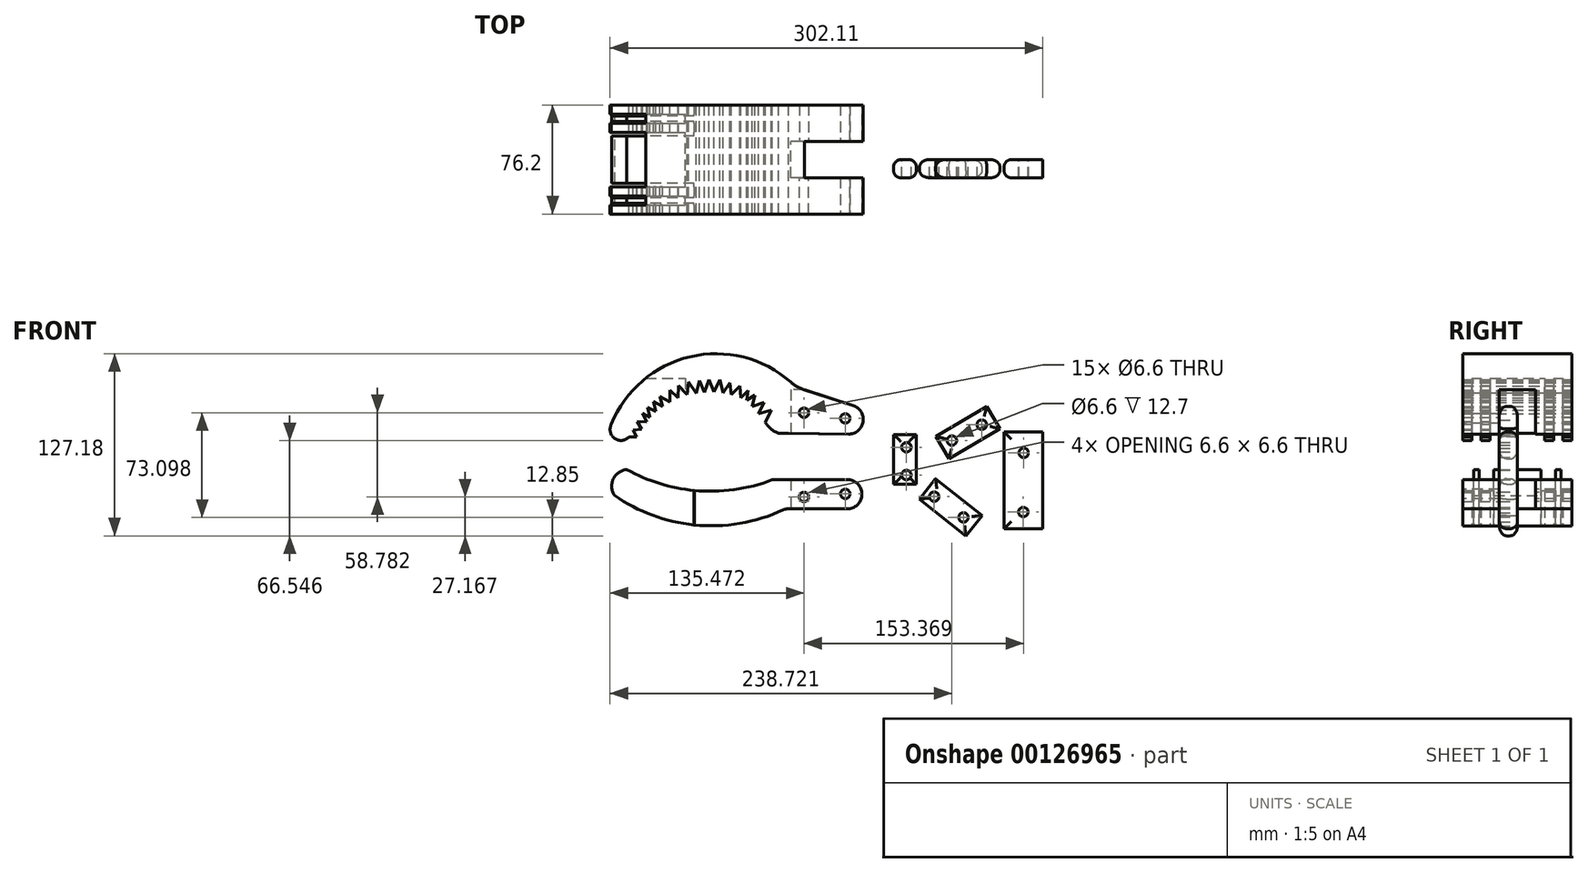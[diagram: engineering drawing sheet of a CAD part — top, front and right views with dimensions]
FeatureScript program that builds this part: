
annotation { "Feature Type Name" : "Feature", "Feature Type Description" : "" }
export const myFeature = defineFeature(function(context is Context, id is Id, definition is map)
    precondition{}
    {
        {
            var Q0;
            Q0=qCreatedBy(makeId("Front.planeOp"),FACE);
            var sketch = newSketch(context, id + "F0", { "sketchPlane" : qUnion([Q0])});
            skCircle(sketch, "E0", {"center": v(-122.1, 20.92) * mm, "radius": 7.64 * mm});
            skCircle(sketch, "E1", {"center": v(36.86, 27.9) * mm, "radius": 10.23 * mm});
            skArc(sketch, "E2", {"start": v(-123.71, 13.46) * mm, "mid": v(-118.67, 12.71) * mm, "end": v(-113.57, 12.7) * mm});
            skLineSegment(sketch, "E3", {"start": v(-113.57, 12.7) * mm, "end": v(-116.58, 15.66) * mm});
            skLineSegment(sketch, "E4", {"start": v(-116.58, 15.66) * mm, "end": v(-111.04, 15.66) * mm});
            skLineSegment(sketch, "E5", {"start": v(-111.04, 15.66) * mm, "end": v(-113.69, 20.54) * mm});
            skLineSegment(sketch, "E6", {"start": v(-113.69, 20.54) * mm, "end": v(-107.75, 21.21) * mm});
            skLineSegment(sketch, "E7", {"start": v(-107.75, 21.21) * mm, "end": v(-110.68, 26.41) * mm});
            skLineSegment(sketch, "E8", {"start": v(-110.68, 26.41) * mm, "end": v(-104.13, 26.23) * mm});
            skLineSegment(sketch, "E9", {"start": v(-104.13, 26.23) * mm, "end": v(-107.13, 32.13) * mm});
            skLineSegment(sketch, "E10", {"start": v(-107.13, 32.13) * mm, "end": v(-101.9, 29.23) * mm});
            skLineSegment(sketch, "E11", {"start": v(-101.9, 29.23) * mm, "end": v(-103.63, 36.21) * mm});
            skLineSegment(sketch, "E12", {"start": v(-103.63, 36.21) * mm, "end": v(-97.74, 33.43) * mm});
            skLineSegment(sketch, "E13", {"start": v(-97.74, 33.43) * mm, "end": v(-99.24, 40.39) * mm});
            skLineSegment(sketch, "E14", {"start": v(-99.24, 40.39) * mm, "end": v(-93.17, 36.84) * mm});
            skLineSegment(sketch, "E15", {"start": v(-93.17, 36.84) * mm, "end": v(-94.84, 44.07) * mm});
            skLineSegment(sketch, "E16", {"start": v(-94.84, 44.07) * mm, "end": v(-87.85, 40.25) * mm});
            skLineSegment(sketch, "E17", {"start": v(-87.85, 40.25) * mm, "end": v(-87.85, 48.47) * mm});
            skLineSegment(sketch, "E18", {"start": v(-87.85, 48.47) * mm, "end": v(-82.13, 43.15) * mm});
            skLineSegment(sketch, "E19", {"start": v(-82.13, 43.15) * mm, "end": v(-81.85, 51.6) * mm});
            skLineSegment(sketch, "E20", {"start": v(-81.85, 51.6) * mm, "end": v(-76.02, 45.36) * mm});
            skLineSegment(sketch, "E21", {"start": v(-76.02, 45.36) * mm, "end": v(-75.03, 53.99) * mm});
            skLineSegment(sketch, "E22", {"start": v(-75.03, 53.99) * mm, "end": v(-69.61, 46.28) * mm});
            skLineSegment(sketch, "E23", {"start": v(-69.61, 46.28) * mm, "end": v(-67.33, 55.15) * mm});
            skLineSegment(sketch, "E24", {"start": v(-67.33, 55.15) * mm, "end": v(-63.89, 46.93) * mm});
            skLineSegment(sketch, "E25", {"start": v(-63.89, 46.93) * mm, "end": v(-60.58, 55.83) * mm});
            skLineSegment(sketch, "E26", {"start": v(-60.58, 55.83) * mm, "end": v(-57.03, 47.07) * mm});
            skLineSegment(sketch, "E27", {"start": v(-57.03, 47.07) * mm, "end": v(-53, 55.7) * mm});
            skLineSegment(sketch, "E28", {"start": v(-53, 55.7) * mm, "end": v(-50.8, 46.52) * mm});
            skLineSegment(sketch, "E29", {"start": v(-50.8, 46.52) * mm, "end": v(-45.92, 53.65) * mm});
            skLineSegment(sketch, "E30", {"start": v(-45.92, 53.65) * mm, "end": v(-44.96, 45.16) * mm});
            skLineSegment(sketch, "E31", {"start": v(-44.96, 45.16) * mm, "end": v(-39.17, 51.16) * mm});
            skLineSegment(sketch, "E32", {"start": v(-39.17, 51.16) * mm, "end": v(-38.42, 43.15) * mm});
            skLineSegment(sketch, "E33", {"start": v(-38.42, 43.15) * mm, "end": v(-33.4, 47.99) * mm});
            skLineSegment(sketch, "E34", {"start": v(-33.4, 47.99) * mm, "end": v(-34.22, 41.27) * mm});
            skLineSegment(sketch, "E35", {"start": v(-34.22, 41.27) * mm, "end": v(-28.5, 44.82) * mm});
            skLineSegment(sketch, "E36", {"start": v(-28.5, 44.82) * mm, "end": v(-30.34, 36.9) * mm});
            skLineSegment(sketch, "E37", {"start": v(-30.34, 36.9) * mm, "end": v(-22.2, 39.85) * mm});
            skLineSegment(sketch, "E38", {"start": v(-22.2, 39.85) * mm, "end": v(-26.04, 31.96) * mm});
            skLineSegment(sketch, "E39", {"start": v(-26.04, 31.96) * mm, "end": v(-17.22, 34.47) * mm});
            skLineSegment(sketch, "E40", {"start": v(-17.22, 34.47) * mm, "end": v(-21.27, 26) * mm});
            skLineSegment(sketch, "E41", {"start": v(-11.97, 18.3) * mm, "end": v(-5.02, 18.3) * mm});
            skLineSegment(sketch, "E42", {"start": v(-5.02, 18.3) * mm, "end": v(36.71, 17.67) * mm});
            skArc(sketch, "E43", {"start": v(-3.6, 54) * mm, "mid": v(-73.85, 71.74) * mm, "end": v(-128.83, 24.54) * mm});
            skLineSegment(sketch, "E44", {"start": v(5.42, 48.84) * mm, "end": v(40.02, 37.63) * mm});
            skPoint(sketch, "E45.visualSharp", {"position": v(0, 50.6) * mm});
            skArc(sketch, "E45.filletArc", {"start": v(-3.6, 54) * mm, "mid": v(0.64, 50.96) * mm, "end": v(5.42, 48.84) * mm});
            skArc(sketch, "E46", {"start": v(-21.27, 26) * mm, "mid": v(-17.33, 21.28) * mm, "end": v(-11.97, 18.3) * mm});
            skArc(sketch, "E47", {"start": v(-118, -7.08) * mm, "mid": v(-127.5, -13.68) * mm, "end": v(-126.5, -25.21) * mm});
            skArc(sketch, "E48", {"start": v(-118, -7.08) * mm, "mid": v(-67.99, -21.92) * mm, "end": v(-16.4, -14.29) * mm});
            skArc(sketch, "E49", {"start": v(-126.5, -25.21) * mm, "mid": v(-68.9, -45.94) * mm, "end": v(-8.64, -35.17) * mm});
            skLineSegment(sketch, "E50", {"start": v(-16.4, -14.29) * mm, "end": v(37.68, -14.29) * mm});
            skLineSegment(sketch, "E51", {"start": v(-5.95, -34.57) * mm, "end": v(35.99, -34.57) * mm});
            skArc(sketch, "E52", {"start": v(35.99, -34.57) * mm, "mid": v(46.16, -25.2) * mm, "end": v(37.68, -14.29) * mm});
            skLineSegment(sketch, "E53.bottom", {"start": v(84.1, -17.42) * mm, "end": v(68.24, -17.42) * mm});
            skLineSegment(sketch, "E53.top", {"start": v(84.1, 17.42) * mm, "end": v(68.24, 17.42) * mm});
            skLineSegment(sketch, "E53.left", {"start": v(84.1, -17.42) * mm, "end": v(84.1, 17.42) * mm});
            skLineSegment(sketch, "E53.right", {"start": v(68.24, -17.42) * mm, "end": v(68.24, 17.42) * mm});
            skPoint(sketch, "E53.middle", {"position": v(76.17, 0) * mm});
            skLineSegment(sketch, "E54.bottom", {"start": v(172.37, 19.24) * mm, "end": v(145.4, 19.24) * mm});
            skLineSegment(sketch, "E54.top", {"start": v(172.37, -48.32) * mm, "end": v(145.4, -48.32) * mm});
            skLineSegment(sketch, "E54.left", {"start": v(172.37, 19.24) * mm, "end": v(172.37, -48.32) * mm});
            skLineSegment(sketch, "E54.right", {"start": v(145.4, 19.24) * mm, "end": v(145.4, -48.32) * mm});
            skPoint(sketch, "E54.middle", {"position": v(158.88, -14.54) * mm});
            skLineSegment(sketch, "E55.top", {"start": v(133.36, 36.98) * mm, "end": v(142.54, 21.29) * mm});
            skLineSegment(sketch, "E55.left", {"start": v(97.73, 16.15) * mm, "end": v(133.36, 36.98) * mm});
            skLineSegment(sketch, "E55.right", {"start": v(106.9, 0.45) * mm, "end": v(142.54, 21.29) * mm});
            skLineSegment(sketch, "E56.bottom", {"start": v(118.74, -53.35) * mm, "end": v(130.01, -39.1) * mm});
            skLineSegment(sketch, "E56.top", {"start": v(86.36, -27.76) * mm, "end": v(97.63, -13.5) * mm});
            skLineSegment(sketch, "E56.left", {"start": v(118.74, -53.35) * mm, "end": v(86.36, -27.76) * mm});
            skLineSegment(sketch, "E56.right", {"start": v(130.01, -39.1) * mm, "end": v(97.63, -13.5) * mm});
            skLineSegment(sketch, "E57", {"start": v(97.73, 16.15) * mm, "end": v(106.9, 0.45) * mm});
            skPoint(sketch, "E58.visualSharp", {"position": v(-7.38, -34.57) * mm});
            skArc(sketch, "E58.filletArc", {"start": v(-5.95, -34.57) * mm, "mid": v(-7.33, -34.72) * mm, "end": v(-8.64, -35.17) * mm});
            skPoint(sketch, "E59", {"position": v(5.73, 32.6) * mm});
            skPoint(sketch, "E60", {"position": v(5.73, -26.18) * mm});
            skPoint(sketch, "E61", {"position": v(77.23, 8.5) * mm});
            skPoint(sketch, "E62", {"position": v(77.23, -10.88) * mm});
            skPoint(sketch, "E63", {"position": v(108.98, 13.2) * mm});
            skPoint(sketch, "E64", {"position": v(129.86, 24.28) * mm});
            skPoint(sketch, "E65", {"position": v(96.62, -26.01) * mm});
            skPoint(sketch, "E66", {"position": v(117.08, -40.5) * mm});
            skPoint(sketch, "E67", {"position": v(159.1, 4.57) * mm});
            skPoint(sketch, "E68", {"position": v(158.87, -36.77) * mm});
            skSolve(sketch);
        }
        {
            var Q0;
            Q0=qCreatedBy(makeId("Right.planeOp"),FACE);
            var sketch = newSketch(context, id + "F1", { "sketchPlane" : qUnion([Q0])});
            skLineSegment(sketch, "E69.bottom", {"start": v(19.05, 29.98) * mm, "end": v(-19.05, 29.98) * mm});
            skLineSegment(sketch, "E69.top", {"start": v(19.05, -29.98) * mm, "end": v(-19.05, -29.98) * mm});
            skLineSegment(sketch, "E69.left", {"start": v(19.05, 29.98) * mm, "end": v(19.05, -29.98) * mm});
            skLineSegment(sketch, "E69.right", {"start": v(-19.05, 29.98) * mm, "end": v(-19.05, -29.98) * mm});
            skPoint(sketch, "E69.middle", {"position": v(0, 0) * mm});
            skLineSegment(sketch, "E70.bottom", {"start": v(-31.75, 29.98) * mm, "end": v(-25.4, 29.98) * mm});
            skLineSegment(sketch, "E70.top", {"start": v(-31.75, -29.98) * mm, "end": v(-25.4, -29.98) * mm});
            skLineSegment(sketch, "E70.left", {"start": v(-31.75, 29.98) * mm, "end": v(-31.75, -29.98) * mm});
            skLineSegment(sketch, "E70.right", {"start": v(-25.4, 29.98) * mm, "end": v(-25.4, -29.98) * mm});
            skPoint(sketch, "E70.middle", {"position": v(-28.58, 0) * mm});
            skLineSegment(sketch, "E71.bottom", {"start": v(25.4, 29.98) * mm, "end": v(31.75, 29.98) * mm});
            skLineSegment(sketch, "E71.top", {"start": v(25.4, -29.98) * mm, "end": v(31.75, -29.98) * mm});
            skLineSegment(sketch, "E71.left", {"start": v(25.4, 29.98) * mm, "end": v(25.4, -29.98) * mm});
            skLineSegment(sketch, "E71.right", {"start": v(31.75, 29.98) * mm, "end": v(31.75, -29.98) * mm});
            skPoint(sketch, "E71.middle", {"position": v(28.58, 0) * mm});
            skLineSegment(sketch, "E72", {"start": v(25.4, 29.98) * mm, "end": v(19.05, 29.98) * mm});
            skLineSegment(sketch, "E73", {"start": v(25.4, -29.98) * mm, "end": v(19.05, -29.98) * mm});
            skLineSegment(sketch, "E74", {"start": v(-19.05, -29.98) * mm, "end": v(-25.4, -29.98) * mm});
            skLineSegment(sketch, "E75", {"start": v(-19.05, 29.98) * mm, "end": v(-25.4, 29.98) * mm});
            skLineSegment(sketch, "E76", {"start": v(31.75, 29.98) * mm, "end": v(38.1, 29.98) * mm});
            skLineSegment(sketch, "E77", {"start": v(38.1, 29.98) * mm, "end": v(38.1, -29.98) * mm});
            skLineSegment(sketch, "E78", {"start": v(38.1, -29.98) * mm, "end": v(31.75, -29.98) * mm});
            skLineSegment(sketch, "E79", {"start": v(-31.75, 29.98) * mm, "end": v(-38.1, 29.98) * mm});
            skLineSegment(sketch, "E80", {"start": v(-38.1, 29.98) * mm, "end": v(-38.1, -29.98) * mm});
            skLineSegment(sketch, "E81", {"start": v(-38.1, -29.98) * mm, "end": v(-31.75, -29.98) * mm});
            skSolve(sketch);
        }
        {
            var Q0;
            {var subQ0=sQuery(id+"F0.wireOp",EDGE,"E5");Q0=makeQuery(id+"F0.imprint","IMPRINT",FACE,{"disambiguationData":[TD([[makeQuery(id+"F0.imprint","IMPRINT",EDGE,{"derivedFrom":subQ0}),1.0]])]});}
            var Q1;
            {var subQ3=sQuery(id+"F0.wireOp",EDGE,"E0");var subQ5=makeQuery(id+"F0.imprint","INTERSECT",VERTEX,{"derivedFrom":[subQ3,sQuery(id+"F0.wireOp",EDGE,"E2")]});Q1=makeQuery(id+"F0.imprint","IMPRINT",FACE,{"disambiguationData":[TD([[makeQuery(id+"F0.imprint","IMPRINT",EDGE,{"disambiguationData":[TD([[subQ5,1.0]])],"derivedFrom":subQ3}),1.0]])]});}
            var Q2;
            {var subQ0=sQuery(id+"F0.wireOp",EDGE,"E1");var subQ1=makeQuery(id+"F0.imprint","INTERSECT",VERTEX,{"derivedFrom":[subQ0,sQuery(id+"F0.wireOp",EDGE,"E42")]});Q2=makeQuery(id+"F0.imprint","IMPRINT",FACE,{"disambiguationData":[TD([[makeQuery(id+"F0.imprint","IMPRINT",EDGE,{"disambiguationData":[TD([[subQ1,1.0]])],"derivedFrom":subQ0}),1.0]])]});}
            extrude(context, id + "F2", {"entities" : qUnion([Q0, Q1, Q2]), "endBound" : BoundingType.SYMMETRIC, "depth" : 76.2 * mm});
        }
        {
            var Q0;
            Q0=makeQuery(id+"F0.imprint","IMPRINT",FACE,{"disambiguationData":[TD([[makeQuery(id+"F0.imprint","IMPRINT",EDGE,{"derivedFrom":sQuery(id+"F0.wireOp",EDGE,"E47")}),1.0]])]});
            extrude(context, id + "F3", {"entities" : qUnion([Q0]), "endBound" : BoundingType.SYMMETRIC, "depth" : 76.2 * mm});
        }
        {
            var Q0;
            Q0=makeQuery(id+"F1.imprint","IMPRINT",FACE,{"disambiguationData":[TD([[makeQuery(id+"F1.imprint","IMPRINT",EDGE,{"derivedFrom":sQuery(id+"F1.wireOp",EDGE,"E70.bottom")}),-1.0]])]});
            var Q1;
            Q1=makeQuery(id+"F1.imprint","IMPRINT",FACE,{"disambiguationData":[TD([[makeQuery(id+"F1.imprint","IMPRINT",EDGE,{"derivedFrom":sQuery(id+"F1.wireOp",EDGE,"E71.bottom")}),-1.0]])]});
            var Q2;
            Q2=makeQuery(id+"F1.imprint","IMPRINT",FACE,{"disambiguationData":[TD([[makeQuery(id+"F1.imprint","IMPRINT",EDGE,{"derivedFrom":sQuery(id+"F1.wireOp",EDGE,"E69.bottom")}),1.0]])]});
            extrude(context, id + "F4", {"entities" : qUnion([Q0, Q1, Q2]), "endBound" : BoundingType.SYMMETRIC, "oppositeDirection" : true, "depth" : 101.6 * mm});
        }
        {
            var Q0;
            Q0=makeQuery(id+"F4.opExtrude","SWEPT_BODY",BODY,{"disambiguationData":[OSD([sQuery(id+"F1.wireOp",EDGE,"E71.bottom"),sQuery(id+"F1.wireOp",EDGE,"E71.top"),sQuery(id+"F1.wireOp",EDGE,"E71.left"),sQuery(id+"F1.wireOp",EDGE,"E71.right")])]});
            var Q1;
            Q1=makeQuery(id+"F4.opExtrude","SWEPT_BODY",BODY,{"disambiguationData":[OSD([sQuery(id+"F1.wireOp",EDGE,"E69.bottom"),sQuery(id+"F1.wireOp",EDGE,"E69.top"),sQuery(id+"F1.wireOp",EDGE,"E69.left"),sQuery(id+"F1.wireOp",EDGE,"E69.right")])]});
            var Q2;
            Q2=makeQuery(id+"F4.opExtrude","SWEPT_BODY",BODY,{"disambiguationData":[OSD([sQuery(id+"F1.wireOp",EDGE,"E70.bottom"),sQuery(id+"F1.wireOp",EDGE,"E70.top"),sQuery(id+"F1.wireOp",EDGE,"E70.left"),sQuery(id+"F1.wireOp",EDGE,"E70.right")])]});
            transform(context, id + "F5", {"entities" : qUnion([Q0, Q1, Q2]), "transformType" : TransformType.TRANSLATION_3D, "dx" : -127.84 * mm, "dy" : 0 * mm, "dz" : 26.7 * mm, "makeCopy" : false});
        }
        {
            var Q0;
            Q0=makeQuery(id+"F4.opExtrude","SWEPT_BODY",BODY,{"disambiguationData":[OSD([sQuery(id+"F1.wireOp",EDGE,"E71.bottom"),sQuery(id+"F1.wireOp",EDGE,"E71.top"),sQuery(id+"F1.wireOp",EDGE,"E71.left"),sQuery(id+"F1.wireOp",EDGE,"E71.right")])]});
            var Q1;
            Q1=makeQuery(id+"F4.opExtrude","SWEPT_BODY",BODY,{"disambiguationData":[OSD([sQuery(id+"F1.wireOp",EDGE,"E69.bottom"),sQuery(id+"F1.wireOp",EDGE,"E69.top"),sQuery(id+"F1.wireOp",EDGE,"E69.left"),sQuery(id+"F1.wireOp",EDGE,"E69.right")])]});
            var Q2;
            Q2=makeQuery(id+"F4.opExtrude","SWEPT_BODY",BODY,{"disambiguationData":[OSD([sQuery(id+"F1.wireOp",EDGE,"E70.bottom"),sQuery(id+"F1.wireOp",EDGE,"E70.top"),sQuery(id+"F1.wireOp",EDGE,"E70.left"),sQuery(id+"F1.wireOp",EDGE,"E70.right")])]});
            var Q3;
            Q3=makeQuery(id+"F2.opExtrude","SWEPT_BODY",BODY,{"disambiguationData":[OSD([sQuery(id+"F0.wireOp",EDGE,"E0"),sQuery(id+"F0.wireOp",EDGE,"E1"),sQuery(id+"F0.wireOp",EDGE,"E3"),sQuery(id+"F0.wireOp",EDGE,"E4"),sQuery(id+"F0.wireOp",EDGE,"E5"),sQuery(id+"F0.wireOp",EDGE,"E6"),sQuery(id+"F0.wireOp",EDGE,"E7"),sQuery(id+"F0.wireOp",EDGE,"E8"),sQuery(id+"F0.wireOp",EDGE,"E9"),sQuery(id+"F0.wireOp",EDGE,"E10"),sQuery(id+"F0.wireOp",EDGE,"E11"),sQuery(id+"F0.wireOp",EDGE,"E12"),sQuery(id+"F0.wireOp",EDGE,"E13"),sQuery(id+"F0.wireOp",EDGE,"E14"),sQuery(id+"F0.wireOp",EDGE,"E15"),sQuery(id+"F0.wireOp",EDGE,"E16"),sQuery(id+"F0.wireOp",EDGE,"E17"),sQuery(id+"F0.wireOp",EDGE,"E18"),sQuery(id+"F0.wireOp",EDGE,"E19"),sQuery(id+"F0.wireOp",EDGE,"E20"),sQuery(id+"F0.wireOp",EDGE,"E21"),sQuery(id+"F0.wireOp",EDGE,"E22"),sQuery(id+"F0.wireOp",EDGE,"E23"),sQuery(id+"F0.wireOp",EDGE,"E24"),sQuery(id+"F0.wireOp",EDGE,"E25"),sQuery(id+"F0.wireOp",EDGE,"E26"),sQuery(id+"F0.wireOp",EDGE,"E27"),sQuery(id+"F0.wireOp",EDGE,"E28"),sQuery(id+"F0.wireOp",EDGE,"E29"),sQuery(id+"F0.wireOp",EDGE,"E30"),sQuery(id+"F0.wireOp",EDGE,"E31"),sQuery(id+"F0.wireOp",EDGE,"E32"),sQuery(id+"F0.wireOp",EDGE,"E33"),sQuery(id+"F0.wireOp",EDGE,"E34"),sQuery(id+"F0.wireOp",EDGE,"E35"),sQuery(id+"F0.wireOp",EDGE,"E36"),sQuery(id+"F0.wireOp",EDGE,"E37"),sQuery(id+"F0.wireOp",EDGE,"E38"),sQuery(id+"F0.wireOp",EDGE,"E39"),sQuery(id+"F0.wireOp",EDGE,"E40"),sQuery(id+"F0.wireOp",EDGE,"E41"),sQuery(id+"F0.wireOp",EDGE,"E42"),sQuery(id+"F0.wireOp",EDGE,"E43"),sQuery(id+"F0.wireOp",EDGE,"E44"),sQuery(id+"F0.wireOp",EDGE,"E45.filletArc"),sQuery(id+"F0.wireOp",EDGE,"E46")])]});
            booleanBodies(context, id + "F6", {"operationType" : BooleanOperationType.SUBTRACTION, "tools" : qUnion([Q0, Q1, Q2]), "targets" : qUnion([Q3])});
        }
        {
            var Q0;
            Q0=makeQuery(id+"F1.imprint","IMPRINT",FACE,{"disambiguationData":[TD([[makeQuery(id+"F1.imprint","IMPRINT",EDGE,{"derivedFrom":sQuery(id+"F1.wireOp",EDGE,"E71.right")}),1.0]])]});
            var Q1;
            Q1=makeQuery(id+"F1.imprint","IMPRINT",FACE,{"disambiguationData":[TD([[makeQuery(id+"F1.imprint","IMPRINT",EDGE,{"derivedFrom":sQuery(id+"F1.wireOp",EDGE,"E69.left")}),1.0]])]});
            var Q2;
            Q2=makeQuery(id+"F1.imprint","IMPRINT",FACE,{"disambiguationData":[TD([[makeQuery(id+"F1.imprint","IMPRINT",EDGE,{"derivedFrom":sQuery(id+"F1.wireOp",EDGE,"E69.right")}),-1.0]])]});
            var Q3;
            Q3=makeQuery(id+"F1.imprint","IMPRINT",FACE,{"disambiguationData":[TD([[makeQuery(id+"F1.imprint","IMPRINT",EDGE,{"derivedFrom":sQuery(id+"F1.wireOp",EDGE,"E70.left")}),-1.0]])]});
            extrude(context, id + "F7", {"entities" : qUnion([Q0, Q1, Q2, Q3]), "depth" : 101.6 * mm});
        }
        {
            var Q0;
            Q0=makeQuery(id+"F7.opExtrude","SWEPT_BODY",BODY,{"disambiguationData":[OSD([sQuery(id+"F1.wireOp",EDGE,"E70.left"),sQuery(id+"F1.wireOp",EDGE,"E79"),sQuery(id+"F1.wireOp",EDGE,"E80"),sQuery(id+"F1.wireOp",EDGE,"E81")])]});
            var Q1;
            Q1=makeQuery(id+"F7.opExtrude","SWEPT_BODY",BODY,{"disambiguationData":[OSD([sQuery(id+"F1.wireOp",EDGE,"E69.right"),sQuery(id+"F1.wireOp",EDGE,"E70.right"),sQuery(id+"F1.wireOp",EDGE,"E74"),sQuery(id+"F1.wireOp",EDGE,"E75")])]});
            var Q2;
            Q2=makeQuery(id+"F7.opExtrude","SWEPT_BODY",BODY,{"disambiguationData":[OSD([sQuery(id+"F1.wireOp",EDGE,"E71.right"),sQuery(id+"F1.wireOp",EDGE,"E76"),sQuery(id+"F1.wireOp",EDGE,"E77"),sQuery(id+"F1.wireOp",EDGE,"E78")])]});
            var Q3;
            Q3=makeQuery(id+"F7.opExtrude","SWEPT_BODY",BODY,{"disambiguationData":[OSD([sQuery(id+"F1.wireOp",EDGE,"E69.left"),sQuery(id+"F1.wireOp",EDGE,"E71.left"),sQuery(id+"F1.wireOp",EDGE,"E72"),sQuery(id+"F1.wireOp",EDGE,"E73")])]});
            transform(context, id + "F8", {"entities" : qUnion([Q0, Q1, Q2, Q3]), "transformType" : TransformType.TRANSLATION_3D, "dx" : -172.57 * mm, "dy" : 0 * mm, "dz" : -27.78 * mm, "makeCopy" : false});
        }
        {
            var Q0;
            Q0=makeQuery(id+"F7.opExtrude","SWEPT_BODY",BODY,{"disambiguationData":[OSD([sQuery(id+"F1.wireOp",EDGE,"E71.right"),sQuery(id+"F1.wireOp",EDGE,"E76"),sQuery(id+"F1.wireOp",EDGE,"E77"),sQuery(id+"F1.wireOp",EDGE,"E78")])]});
            var Q1;
            Q1=makeQuery(id+"F7.opExtrude","SWEPT_BODY",BODY,{"disambiguationData":[OSD([sQuery(id+"F1.wireOp",EDGE,"E69.left"),sQuery(id+"F1.wireOp",EDGE,"E71.left"),sQuery(id+"F1.wireOp",EDGE,"E72"),sQuery(id+"F1.wireOp",EDGE,"E73")])]});
            var Q2;
            Q2=makeQuery(id+"F7.opExtrude","SWEPT_BODY",BODY,{"disambiguationData":[OSD([sQuery(id+"F1.wireOp",EDGE,"E69.right"),sQuery(id+"F1.wireOp",EDGE,"E70.right"),sQuery(id+"F1.wireOp",EDGE,"E74"),sQuery(id+"F1.wireOp",EDGE,"E75")])]});
            var Q3;
            Q3=makeQuery(id+"F7.opExtrude","SWEPT_BODY",BODY,{"disambiguationData":[OSD([sQuery(id+"F1.wireOp",EDGE,"E70.left"),sQuery(id+"F1.wireOp",EDGE,"E79"),sQuery(id+"F1.wireOp",EDGE,"E80"),sQuery(id+"F1.wireOp",EDGE,"E81")])]});
            var Q4;
            Q4=makeQuery(id+"F3.opExtrude","SWEPT_BODY",BODY,{"disambiguationData":[OSD([sQuery(id+"F0.wireOp",EDGE,"E47"),sQuery(id+"F0.wireOp",EDGE,"E48"),sQuery(id+"F0.wireOp",EDGE,"E49"),sQuery(id+"F0.wireOp",EDGE,"E50"),sQuery(id+"F0.wireOp",EDGE,"E51"),sQuery(id+"F0.wireOp",EDGE,"E52"),sQuery(id+"F0.wireOp",EDGE,"E58.filletArc")])]});
            booleanBodies(context, id + "F9", {"operationType" : BooleanOperationType.SUBTRACTION, "tools" : qUnion([Q0, Q1, Q2, Q3]), "targets" : qUnion([Q4])});
        }
        {
            var Q0;
            Q0=makeQuery(id+"F2.opExtrude","CAP_FACE",FACE,{"disambiguationData":[OSD([sQuery(id+"F0.wireOp",EDGE,"E0"),sQuery(id+"F0.wireOp",EDGE,"E1"),sQuery(id+"F0.wireOp",EDGE,"E3"),sQuery(id+"F0.wireOp",EDGE,"E4"),sQuery(id+"F0.wireOp",EDGE,"E5"),sQuery(id+"F0.wireOp",EDGE,"E6"),sQuery(id+"F0.wireOp",EDGE,"E7"),sQuery(id+"F0.wireOp",EDGE,"E8"),sQuery(id+"F0.wireOp",EDGE,"E9"),sQuery(id+"F0.wireOp",EDGE,"E10"),sQuery(id+"F0.wireOp",EDGE,"E11"),sQuery(id+"F0.wireOp",EDGE,"E12"),sQuery(id+"F0.wireOp",EDGE,"E13"),sQuery(id+"F0.wireOp",EDGE,"E14"),sQuery(id+"F0.wireOp",EDGE,"E15"),sQuery(id+"F0.wireOp",EDGE,"E16"),sQuery(id+"F0.wireOp",EDGE,"E17"),sQuery(id+"F0.wireOp",EDGE,"E18"),sQuery(id+"F0.wireOp",EDGE,"E19"),sQuery(id+"F0.wireOp",EDGE,"E20"),sQuery(id+"F0.wireOp",EDGE,"E21"),sQuery(id+"F0.wireOp",EDGE,"E22"),sQuery(id+"F0.wireOp",EDGE,"E23"),sQuery(id+"F0.wireOp",EDGE,"E24"),sQuery(id+"F0.wireOp",EDGE,"E25"),sQuery(id+"F0.wireOp",EDGE,"E26"),sQuery(id+"F0.wireOp",EDGE,"E27"),sQuery(id+"F0.wireOp",EDGE,"E28"),sQuery(id+"F0.wireOp",EDGE,"E29"),sQuery(id+"F0.wireOp",EDGE,"E30"),sQuery(id+"F0.wireOp",EDGE,"E31"),sQuery(id+"F0.wireOp",EDGE,"E32"),sQuery(id+"F0.wireOp",EDGE,"E33"),sQuery(id+"F0.wireOp",EDGE,"E34"),sQuery(id+"F0.wireOp",EDGE,"E35"),sQuery(id+"F0.wireOp",EDGE,"E36"),sQuery(id+"F0.wireOp",EDGE,"E37"),sQuery(id+"F0.wireOp",EDGE,"E38"),sQuery(id+"F0.wireOp",EDGE,"E39"),sQuery(id+"F0.wireOp",EDGE,"E40"),sQuery(id+"F0.wireOp",EDGE,"E41"),sQuery(id+"F0.wireOp",EDGE,"E42"),sQuery(id+"F0.wireOp",EDGE,"E43"),sQuery(id+"F0.wireOp",EDGE,"E44"),sQuery(id+"F0.wireOp",EDGE,"E45.filletArc"),sQuery(id+"F0.wireOp",EDGE,"E46")])],"isStart":false});
            var sketch = newSketch(context, id + "F10", { "sketchPlane" : qUnion([Q0])});
            skPoint(sketch, "E82", {"position": v(34.51, 28.65) * mm});
            skPoint(sketch, "E83", {"position": v(34.51, -24.1) * mm});
            skSolve(sketch);
        }
        {
            var Q0;
            Q0=sQuery(id+"F10.wireOp",VERTEX,"E82");
            var Q1;
            Q1=sQuery(id+"F10.wireOp",VERTEX,"E83");
            var Q2;
            Q2=makeQuery(id+"F2.opExtrude","SWEPT_BODY",BODY,{"disambiguationData":[OSD([sQuery(id+"F0.wireOp",EDGE,"E0"),sQuery(id+"F0.wireOp",EDGE,"E1"),sQuery(id+"F0.wireOp",EDGE,"E3"),sQuery(id+"F0.wireOp",EDGE,"E4"),sQuery(id+"F0.wireOp",EDGE,"E5"),sQuery(id+"F0.wireOp",EDGE,"E6"),sQuery(id+"F0.wireOp",EDGE,"E7"),sQuery(id+"F0.wireOp",EDGE,"E8"),sQuery(id+"F0.wireOp",EDGE,"E9"),sQuery(id+"F0.wireOp",EDGE,"E10"),sQuery(id+"F0.wireOp",EDGE,"E11"),sQuery(id+"F0.wireOp",EDGE,"E12"),sQuery(id+"F0.wireOp",EDGE,"E13"),sQuery(id+"F0.wireOp",EDGE,"E14"),sQuery(id+"F0.wireOp",EDGE,"E15"),sQuery(id+"F0.wireOp",EDGE,"E16"),sQuery(id+"F0.wireOp",EDGE,"E17"),sQuery(id+"F0.wireOp",EDGE,"E18"),sQuery(id+"F0.wireOp",EDGE,"E19"),sQuery(id+"F0.wireOp",EDGE,"E20"),sQuery(id+"F0.wireOp",EDGE,"E21"),sQuery(id+"F0.wireOp",EDGE,"E22"),sQuery(id+"F0.wireOp",EDGE,"E23"),sQuery(id+"F0.wireOp",EDGE,"E24"),sQuery(id+"F0.wireOp",EDGE,"E25"),sQuery(id+"F0.wireOp",EDGE,"E26"),sQuery(id+"F0.wireOp",EDGE,"E27"),sQuery(id+"F0.wireOp",EDGE,"E28"),sQuery(id+"F0.wireOp",EDGE,"E29"),sQuery(id+"F0.wireOp",EDGE,"E30"),sQuery(id+"F0.wireOp",EDGE,"E31"),sQuery(id+"F0.wireOp",EDGE,"E32"),sQuery(id+"F0.wireOp",EDGE,"E33"),sQuery(id+"F0.wireOp",EDGE,"E34"),sQuery(id+"F0.wireOp",EDGE,"E35"),sQuery(id+"F0.wireOp",EDGE,"E36"),sQuery(id+"F0.wireOp",EDGE,"E37"),sQuery(id+"F0.wireOp",EDGE,"E38"),sQuery(id+"F0.wireOp",EDGE,"E39"),sQuery(id+"F0.wireOp",EDGE,"E40"),sQuery(id+"F0.wireOp",EDGE,"E41"),sQuery(id+"F0.wireOp",EDGE,"E42"),sQuery(id+"F0.wireOp",EDGE,"E43"),sQuery(id+"F0.wireOp",EDGE,"E44"),sQuery(id+"F0.wireOp",EDGE,"E45.filletArc"),sQuery(id+"F0.wireOp",EDGE,"E46")])]});
            var Q3;
            Q3=makeQuery(id+"F3.opExtrude","SWEPT_BODY",BODY,{"disambiguationData":[OSD([sQuery(id+"F0.wireOp",EDGE,"E47"),sQuery(id+"F0.wireOp",EDGE,"E48"),sQuery(id+"F0.wireOp",EDGE,"E49"),sQuery(id+"F0.wireOp",EDGE,"E50"),sQuery(id+"F0.wireOp",EDGE,"E51"),sQuery(id+"F0.wireOp",EDGE,"E52"),sQuery(id+"F0.wireOp",EDGE,"E58.filletArc")])]});
            hole(context, id + "F11", {"style" : HoleStyle.SIMPLE, "endStyle" : HoleEndStyle.THROUGH, "holeDiameter" : 6.6 * mm, "locations" : qUnion([Q0, Q1]), "scope" : qUnion([Q2, Q3]), "isTappedThrough" : true});
        }
        {
            var Q0;
            Q0=qCreatedBy(makeId("Right.planeOp"),FACE);
            var sketch = newSketch(context, id + "F12", { "sketchPlane" : qUnion([Q0])});
            skLineSegment(sketch, "E84.bottom", {"start": v(12.7, 46.9) * mm, "end": v(-12.7, 46.9) * mm});
            skLineSegment(sketch, "E84.top", {"start": v(12.7, -46.9) * mm, "end": v(-12.7, -46.9) * mm});
            skLineSegment(sketch, "E84.left", {"start": v(12.7, 46.9) * mm, "end": v(12.7, -46.9) * mm});
            skLineSegment(sketch, "E84.right", {"start": v(-12.7, 46.9) * mm, "end": v(-12.7, -46.9) * mm});
            skPoint(sketch, "E84.middle", {"position": v(0, 0) * mm});
            skSolve(sketch);
        }
        {
            var Q0;
            Q0=makeQuery(id+"F12.imprint","IMPRINT",FACE,{"disambiguationData":[TD([[makeQuery(id+"F12.imprint","IMPRINT",EDGE,{"derivedFrom":sQuery(id+"F12.wireOp",EDGE,"E84.bottom")}),1.0]])]});
            extrude(context, id + "F13", {"entities" : qUnion([Q0]), "endBound" : BoundingType.SYMMETRIC, "depth" : 50.8 * mm});
        }
        {
            var Q0;
            Q0=makeQuery(id+"F13.opExtrude","SWEPT_BODY",BODY,{"disambiguationData":[OSD([sQuery(id+"F12.wireOp",EDGE,"E84.bottom"),sQuery(id+"F12.wireOp",EDGE,"E84.top"),sQuery(id+"F12.wireOp",EDGE,"E84.left"),sQuery(id+"F12.wireOp",EDGE,"E84.right")])]});
            transform(context, id + "F14", {"entities" : qUnion([Q0]), "transformType" : TransformType.TRANSLATION_3D, "dx" : 21.75 * mm, "dy" : 0 * mm, "dz" : 1.8 * mm, "makeCopy" : false});
        }
        {
            var Q0;
            Q0=makeQuery(id+"F13.opExtrude","SWEPT_BODY",BODY,{"disambiguationData":[OSD([sQuery(id+"F12.wireOp",EDGE,"E84.bottom"),sQuery(id+"F12.wireOp",EDGE,"E84.top"),sQuery(id+"F12.wireOp",EDGE,"E84.left"),sQuery(id+"F12.wireOp",EDGE,"E84.right")])]});
            var Q1;
            Q1=makeQuery(id+"F2.opExtrude","SWEPT_BODY",BODY,{"disambiguationData":[OSD([sQuery(id+"F0.wireOp",EDGE,"E0"),sQuery(id+"F0.wireOp",EDGE,"E1"),sQuery(id+"F0.wireOp",EDGE,"E3"),sQuery(id+"F0.wireOp",EDGE,"E4"),sQuery(id+"F0.wireOp",EDGE,"E5"),sQuery(id+"F0.wireOp",EDGE,"E6"),sQuery(id+"F0.wireOp",EDGE,"E7"),sQuery(id+"F0.wireOp",EDGE,"E8"),sQuery(id+"F0.wireOp",EDGE,"E9"),sQuery(id+"F0.wireOp",EDGE,"E10"),sQuery(id+"F0.wireOp",EDGE,"E11"),sQuery(id+"F0.wireOp",EDGE,"E12"),sQuery(id+"F0.wireOp",EDGE,"E13"),sQuery(id+"F0.wireOp",EDGE,"E14"),sQuery(id+"F0.wireOp",EDGE,"E15"),sQuery(id+"F0.wireOp",EDGE,"E16"),sQuery(id+"F0.wireOp",EDGE,"E17"),sQuery(id+"F0.wireOp",EDGE,"E18"),sQuery(id+"F0.wireOp",EDGE,"E19"),sQuery(id+"F0.wireOp",EDGE,"E20"),sQuery(id+"F0.wireOp",EDGE,"E21"),sQuery(id+"F0.wireOp",EDGE,"E22"),sQuery(id+"F0.wireOp",EDGE,"E23"),sQuery(id+"F0.wireOp",EDGE,"E24"),sQuery(id+"F0.wireOp",EDGE,"E25"),sQuery(id+"F0.wireOp",EDGE,"E26"),sQuery(id+"F0.wireOp",EDGE,"E27"),sQuery(id+"F0.wireOp",EDGE,"E28"),sQuery(id+"F0.wireOp",EDGE,"E29"),sQuery(id+"F0.wireOp",EDGE,"E30"),sQuery(id+"F0.wireOp",EDGE,"E31"),sQuery(id+"F0.wireOp",EDGE,"E32"),sQuery(id+"F0.wireOp",EDGE,"E33"),sQuery(id+"F0.wireOp",EDGE,"E34"),sQuery(id+"F0.wireOp",EDGE,"E35"),sQuery(id+"F0.wireOp",EDGE,"E36"),sQuery(id+"F0.wireOp",EDGE,"E37"),sQuery(id+"F0.wireOp",EDGE,"E38"),sQuery(id+"F0.wireOp",EDGE,"E39"),sQuery(id+"F0.wireOp",EDGE,"E40"),sQuery(id+"F0.wireOp",EDGE,"E41"),sQuery(id+"F0.wireOp",EDGE,"E42"),sQuery(id+"F0.wireOp",EDGE,"E43"),sQuery(id+"F0.wireOp",EDGE,"E44"),sQuery(id+"F0.wireOp",EDGE,"E45.filletArc"),sQuery(id+"F0.wireOp",EDGE,"E46")])]});
            var Q2;
            Q2=makeQuery(id+"F3.opExtrude","SWEPT_BODY",BODY,{"disambiguationData":[OSD([sQuery(id+"F0.wireOp",EDGE,"E47"),sQuery(id+"F0.wireOp",EDGE,"E48"),sQuery(id+"F0.wireOp",EDGE,"E49"),sQuery(id+"F0.wireOp",EDGE,"E50"),sQuery(id+"F0.wireOp",EDGE,"E51"),sQuery(id+"F0.wireOp",EDGE,"E52"),sQuery(id+"F0.wireOp",EDGE,"E58.filletArc")])]});
            booleanBodies(context, id + "F15", {"operationType" : BooleanOperationType.SUBTRACTION, "tools" : qUnion([Q0]), "targets" : qUnion([Q1, Q2])});
        }
        {
            var Q0;
            Q0=sQuery(id+"F0.wireOp",VERTEX,"E59");
            var Q1;
            Q1=sQuery(id+"F0.wireOp",VERTEX,"E60");
            var Q2;
            Q2=makeQuery(id+"F2.opExtrude","SWEPT_BODY",BODY,{"disambiguationData":[OSD([sQuery(id+"F0.wireOp",EDGE,"E0"),sQuery(id+"F0.wireOp",EDGE,"E1"),sQuery(id+"F0.wireOp",EDGE,"E3"),sQuery(id+"F0.wireOp",EDGE,"E4"),sQuery(id+"F0.wireOp",EDGE,"E5"),sQuery(id+"F0.wireOp",EDGE,"E6"),sQuery(id+"F0.wireOp",EDGE,"E7"),sQuery(id+"F0.wireOp",EDGE,"E8"),sQuery(id+"F0.wireOp",EDGE,"E9"),sQuery(id+"F0.wireOp",EDGE,"E10"),sQuery(id+"F0.wireOp",EDGE,"E11"),sQuery(id+"F0.wireOp",EDGE,"E12"),sQuery(id+"F0.wireOp",EDGE,"E13"),sQuery(id+"F0.wireOp",EDGE,"E14"),sQuery(id+"F0.wireOp",EDGE,"E15"),sQuery(id+"F0.wireOp",EDGE,"E16"),sQuery(id+"F0.wireOp",EDGE,"E17"),sQuery(id+"F0.wireOp",EDGE,"E18"),sQuery(id+"F0.wireOp",EDGE,"E19"),sQuery(id+"F0.wireOp",EDGE,"E20"),sQuery(id+"F0.wireOp",EDGE,"E21"),sQuery(id+"F0.wireOp",EDGE,"E22"),sQuery(id+"F0.wireOp",EDGE,"E23"),sQuery(id+"F0.wireOp",EDGE,"E24"),sQuery(id+"F0.wireOp",EDGE,"E25"),sQuery(id+"F0.wireOp",EDGE,"E26"),sQuery(id+"F0.wireOp",EDGE,"E27"),sQuery(id+"F0.wireOp",EDGE,"E28"),sQuery(id+"F0.wireOp",EDGE,"E29"),sQuery(id+"F0.wireOp",EDGE,"E30"),sQuery(id+"F0.wireOp",EDGE,"E31"),sQuery(id+"F0.wireOp",EDGE,"E32"),sQuery(id+"F0.wireOp",EDGE,"E33"),sQuery(id+"F0.wireOp",EDGE,"E34"),sQuery(id+"F0.wireOp",EDGE,"E35"),sQuery(id+"F0.wireOp",EDGE,"E36"),sQuery(id+"F0.wireOp",EDGE,"E37"),sQuery(id+"F0.wireOp",EDGE,"E38"),sQuery(id+"F0.wireOp",EDGE,"E39"),sQuery(id+"F0.wireOp",EDGE,"E40"),sQuery(id+"F0.wireOp",EDGE,"E41"),sQuery(id+"F0.wireOp",EDGE,"E42"),sQuery(id+"F0.wireOp",EDGE,"E43"),sQuery(id+"F0.wireOp",EDGE,"E44"),sQuery(id+"F0.wireOp",EDGE,"E45.filletArc"),sQuery(id+"F0.wireOp",EDGE,"E46")])]});
            var Q3;
            Q3=makeQuery(id+"F3.opExtrude","SWEPT_BODY",BODY,{"disambiguationData":[OSD([sQuery(id+"F0.wireOp",EDGE,"E47"),sQuery(id+"F0.wireOp",EDGE,"E48"),sQuery(id+"F0.wireOp",EDGE,"E49"),sQuery(id+"F0.wireOp",EDGE,"E50"),sQuery(id+"F0.wireOp",EDGE,"E51"),sQuery(id+"F0.wireOp",EDGE,"E52"),sQuery(id+"F0.wireOp",EDGE,"E58.filletArc")])]});
            hole(context, id + "F16", {"style" : HoleStyle.SIMPLE, "endStyle" : HoleEndStyle.THROUGH, "oppositeDirection" : true, "holeDiameter" : 6.6 * mm, "locations" : qUnion([Q0, Q1]), "scope" : qUnion([Q2, Q3]), "isTappedThrough" : true});
        }
        {
            var Q0;
            Q0=sQuery(id+"F0.wireOp",VERTEX,"E59");
            var Q1;
            Q1=sQuery(id+"F0.wireOp",VERTEX,"E60");
            var Q2;
            Q2=makeQuery(id+"F2.opExtrude","SWEPT_BODY",BODY,{"disambiguationData":[OSD([sQuery(id+"F0.wireOp",EDGE,"E0"),sQuery(id+"F0.wireOp",EDGE,"E1"),sQuery(id+"F0.wireOp",EDGE,"E3"),sQuery(id+"F0.wireOp",EDGE,"E4"),sQuery(id+"F0.wireOp",EDGE,"E5"),sQuery(id+"F0.wireOp",EDGE,"E6"),sQuery(id+"F0.wireOp",EDGE,"E7"),sQuery(id+"F0.wireOp",EDGE,"E8"),sQuery(id+"F0.wireOp",EDGE,"E9"),sQuery(id+"F0.wireOp",EDGE,"E10"),sQuery(id+"F0.wireOp",EDGE,"E11"),sQuery(id+"F0.wireOp",EDGE,"E12"),sQuery(id+"F0.wireOp",EDGE,"E13"),sQuery(id+"F0.wireOp",EDGE,"E14"),sQuery(id+"F0.wireOp",EDGE,"E15"),sQuery(id+"F0.wireOp",EDGE,"E16"),sQuery(id+"F0.wireOp",EDGE,"E17"),sQuery(id+"F0.wireOp",EDGE,"E18"),sQuery(id+"F0.wireOp",EDGE,"E19"),sQuery(id+"F0.wireOp",EDGE,"E20"),sQuery(id+"F0.wireOp",EDGE,"E21"),sQuery(id+"F0.wireOp",EDGE,"E22"),sQuery(id+"F0.wireOp",EDGE,"E23"),sQuery(id+"F0.wireOp",EDGE,"E24"),sQuery(id+"F0.wireOp",EDGE,"E25"),sQuery(id+"F0.wireOp",EDGE,"E26"),sQuery(id+"F0.wireOp",EDGE,"E27"),sQuery(id+"F0.wireOp",EDGE,"E28"),sQuery(id+"F0.wireOp",EDGE,"E29"),sQuery(id+"F0.wireOp",EDGE,"E30"),sQuery(id+"F0.wireOp",EDGE,"E31"),sQuery(id+"F0.wireOp",EDGE,"E32"),sQuery(id+"F0.wireOp",EDGE,"E33"),sQuery(id+"F0.wireOp",EDGE,"E34"),sQuery(id+"F0.wireOp",EDGE,"E35"),sQuery(id+"F0.wireOp",EDGE,"E36"),sQuery(id+"F0.wireOp",EDGE,"E37"),sQuery(id+"F0.wireOp",EDGE,"E38"),sQuery(id+"F0.wireOp",EDGE,"E39"),sQuery(id+"F0.wireOp",EDGE,"E40"),sQuery(id+"F0.wireOp",EDGE,"E41"),sQuery(id+"F0.wireOp",EDGE,"E42"),sQuery(id+"F0.wireOp",EDGE,"E43"),sQuery(id+"F0.wireOp",EDGE,"E44"),sQuery(id+"F0.wireOp",EDGE,"E45.filletArc"),sQuery(id+"F0.wireOp",EDGE,"E46")])]});
            var Q3;
            Q3=makeQuery(id+"F3.opExtrude","SWEPT_BODY",BODY,{"disambiguationData":[OSD([sQuery(id+"F0.wireOp",EDGE,"E47"),sQuery(id+"F0.wireOp",EDGE,"E48"),sQuery(id+"F0.wireOp",EDGE,"E49"),sQuery(id+"F0.wireOp",EDGE,"E50"),sQuery(id+"F0.wireOp",EDGE,"E51"),sQuery(id+"F0.wireOp",EDGE,"E52"),sQuery(id+"F0.wireOp",EDGE,"E58.filletArc")])]});
            hole(context, id + "F17", {"style" : HoleStyle.SIMPLE, "endStyle" : HoleEndStyle.THROUGH, "holeDiameter" : 6.6 * mm, "locations" : qUnion([Q0, Q1]), "scope" : qUnion([Q2, Q3]), "isTappedThrough" : true});
        }
        {
            var Q0;
            Q0=qCreatedBy(makeId("Right.planeOp"),FACE);
            var sketch = newSketch(context, id + "F18", { "sketchPlane" : qUnion([Q0])});
            skLineSegment(sketch, "E85.bottom", {"start": v(38.1, -46.3) * mm, "end": v(-38.1, -46.3) * mm});
            skLineSegment(sketch, "E85.top", {"start": v(38.1, -5.67) * mm, "end": v(-38.1, -5.67) * mm});
            skLineSegment(sketch, "E85.left", {"start": v(38.1, -46.3) * mm, "end": v(38.1, -5.67) * mm});
            skLineSegment(sketch, "E85.right", {"start": v(-38.1, -46.3) * mm, "end": v(-38.1, -5.67) * mm});
            skLineSegment(sketch, "E86", {"start": v(30.48, -5.67) * mm, "end": v(30.48, -46.3) * mm});
            skLineSegment(sketch, "E87", {"start": v(26.67, -5.67) * mm, "end": v(26.67, -46.3) * mm});
            skLineSegment(sketch, "E88", {"start": v(16.51, -5.67) * mm, "end": v(16.51, -46.3) * mm});
            skLineSegment(sketch, "E89", {"start": v(-16.5, -5.67) * mm, "end": v(-16.5, -46.3) * mm});
            skLineSegment(sketch, "E90", {"start": v(-26.67, -5.67) * mm, "end": v(-26.67, -46.3) * mm});
            skLineSegment(sketch, "E91", {"start": v(-30.48, -5.67) * mm, "end": v(-30.48, -46.3) * mm});
            skSolve(sketch);
        }
        {
            var Q0;
            {var subQ0=sQuery(id+"F18.wireOp",EDGE,"E85.right");Q0=makeQuery(id+"F18.imprint","IMPRINT",FACE,{"disambiguationData":[TD([[makeQuery(id+"F18.imprint","IMPRINT",EDGE,{"derivedFrom":subQ0}),-1.0]])]});}
            var Q1;
            {var subQ0=sQuery(id+"F18.wireOp",EDGE,"E89");Q1=makeQuery(id+"F18.imprint","IMPRINT",FACE,{"disambiguationData":[TD([[makeQuery(id+"F18.imprint","IMPRINT",EDGE,{"derivedFrom":subQ0}),-1.0]])]});}
            var Q2;
            {var subQ0=sQuery(id+"F18.wireOp",EDGE,"E87");Q2=makeQuery(id+"F18.imprint","IMPRINT",FACE,{"disambiguationData":[TD([[makeQuery(id+"F18.imprint","IMPRINT",EDGE,{"derivedFrom":subQ0}),-1.0]])]});}
            var Q3;
            {var subQ0=sQuery(id+"F18.wireOp",EDGE,"E85.left");Q3=makeQuery(id+"F18.imprint","IMPRINT",FACE,{"disambiguationData":[TD([[makeQuery(id+"F18.imprint","IMPRINT",EDGE,{"derivedFrom":subQ0}),1.0]])]});}
            extrude(context, id + "F19", {"entities" : qUnion([Q0, Q1, Q2, Q3]), "depth" : 76.2 * mm});
        }
        {
            var Q0;
            Q0=makeQuery(id+"F19.opExtrude","SWEPT_BODY",BODY,{"disambiguationData":[OSD([sQuery(id+"F18.wireOp",EDGE,"E85.bottom"),sQuery(id+"F18.wireOp",EDGE,"E85.top"),sQuery(id+"F18.wireOp",EDGE,"E89"),sQuery(id+"F18.wireOp",EDGE,"E90")])]});
            var Q1;
            Q1=makeQuery(id+"F19.opExtrude","SWEPT_BODY",BODY,{"disambiguationData":[OSD([sQuery(id+"F18.wireOp",EDGE,"E85.bottom"),sQuery(id+"F18.wireOp",EDGE,"E85.top"),sQuery(id+"F18.wireOp",EDGE,"E87"),sQuery(id+"F18.wireOp",EDGE,"E88")])]});
            var Q2;
            Q2=makeQuery(id+"F19.opExtrude","SWEPT_BODY",BODY,{"disambiguationData":[OSD([sQuery(id+"F18.wireOp",EDGE,"E85.bottom"),sQuery(id+"F18.wireOp",EDGE,"E85.top"),sQuery(id+"F18.wireOp",EDGE,"E85.left"),sQuery(id+"F18.wireOp",EDGE,"E86")])]});
            var Q3;
            Q3=makeQuery(id+"F19.opExtrude","SWEPT_BODY",BODY,{"disambiguationData":[OSD([sQuery(id+"F18.wireOp",EDGE,"E85.bottom"),sQuery(id+"F18.wireOp",EDGE,"E85.top"),sQuery(id+"F18.wireOp",EDGE,"E85.right"),sQuery(id+"F18.wireOp",EDGE,"E91")])]});
            transform(context, id + "F20", {"entities" : qUnion([Q0, Q1, Q2, Q3]), "transformType" : TransformType.TRANSLATION_3D, "dx" : -147.2 * mm, "dy" : 0 * mm, "dz" : 0 * mm, "makeCopy" : false});
        }
        {
            var Q0;
            Q0=makeQuery(id+"F19.opExtrude","SWEPT_BODY",BODY,{"disambiguationData":[OSD([sQuery(id+"F18.wireOp",EDGE,"E85.bottom"),sQuery(id+"F18.wireOp",EDGE,"E85.top"),sQuery(id+"F18.wireOp",EDGE,"E85.left"),sQuery(id+"F18.wireOp",EDGE,"E86")])]});
            var Q1;
            Q1=makeQuery(id+"F19.opExtrude","SWEPT_BODY",BODY,{"disambiguationData":[OSD([sQuery(id+"F18.wireOp",EDGE,"E85.bottom"),sQuery(id+"F18.wireOp",EDGE,"E85.top"),sQuery(id+"F18.wireOp",EDGE,"E87"),sQuery(id+"F18.wireOp",EDGE,"E88")])]});
            var Q2;
            Q2=makeQuery(id+"F19.opExtrude","SWEPT_BODY",BODY,{"disambiguationData":[OSD([sQuery(id+"F18.wireOp",EDGE,"E85.bottom"),sQuery(id+"F18.wireOp",EDGE,"E85.top"),sQuery(id+"F18.wireOp",EDGE,"E89"),sQuery(id+"F18.wireOp",EDGE,"E90")])]});
            var Q3;
            Q3=makeQuery(id+"F19.opExtrude","SWEPT_BODY",BODY,{"disambiguationData":[OSD([sQuery(id+"F18.wireOp",EDGE,"E85.bottom"),sQuery(id+"F18.wireOp",EDGE,"E85.top"),sQuery(id+"F18.wireOp",EDGE,"E85.right"),sQuery(id+"F18.wireOp",EDGE,"E91")])]});
            var Q4;
            Q4=makeQuery(id+"F3.opExtrude","SWEPT_BODY",BODY,{"disambiguationData":[OSD([sQuery(id+"F0.wireOp",EDGE,"E47"),sQuery(id+"F0.wireOp",EDGE,"E48"),sQuery(id+"F0.wireOp",EDGE,"E49"),sQuery(id+"F0.wireOp",EDGE,"E50"),sQuery(id+"F0.wireOp",EDGE,"E51"),sQuery(id+"F0.wireOp",EDGE,"E52"),sQuery(id+"F0.wireOp",EDGE,"E58.filletArc")])]});
            booleanBodies(context, id + "F21", {"operationType" : BooleanOperationType.SUBTRACTION, "tools" : qUnion([Q0, Q1, Q2, Q3]), "targets" : qUnion([Q4])});
        }
        {
            var Q0;
            Q0=makeQuery(id+"F0.imprint","IMPRINT",FACE,{"disambiguationData":[TD([[makeQuery(id+"F0.imprint","IMPRINT",EDGE,{"derivedFrom":sQuery(id+"F0.wireOp",EDGE,"E53.bottom")}),-1.0]])]});
            var Q1;
            Q1=makeQuery(id+"F0.imprint","IMPRINT",FACE,{"disambiguationData":[TD([[makeQuery(id+"F0.imprint","IMPRINT",EDGE,{"derivedFrom":sQuery(id+"F0.wireOp",EDGE,"E55.top")}),-1.0]])]});
            var Q2;
            Q2=makeQuery(id+"F0.imprint","IMPRINT",FACE,{"disambiguationData":[TD([[makeQuery(id+"F0.imprint","IMPRINT",EDGE,{"derivedFrom":sQuery(id+"F0.wireOp",EDGE,"E54.bottom")}),1.0]])]});
            var Q3;
            Q3=makeQuery(id+"F0.imprint","IMPRINT",FACE,{"disambiguationData":[TD([[makeQuery(id+"F0.imprint","IMPRINT",EDGE,{"derivedFrom":sQuery(id+"F0.wireOp",EDGE,"E56.bottom")}),1.0]])]});
            extrude(context, id + "F22", {"entities" : qUnion([Q0, Q1, Q2, Q3]), "depth" : 12.7 * mm});
        }
        {
            var Q0;
            Q0=sQuery(id+"F0.wireOp",VERTEX,"E61");
            var Q1;
            Q1=sQuery(id+"F0.wireOp",VERTEX,"E62");
            var Q2;
            Q2=sQuery(id+"F0.wireOp",VERTEX,"E63");
            var Q3;
            Q3=sQuery(id+"F0.wireOp",VERTEX,"E64");
            var Q4;
            Q4=sQuery(id+"F0.wireOp",VERTEX,"E65");
            var Q5;
            Q5=sQuery(id+"F0.wireOp",VERTEX,"E66");
            var Q6;
            Q6=sQuery(id+"F0.wireOp",VERTEX,"E67");
            var Q7;
            Q7=sQuery(id+"F0.wireOp",VERTEX,"E68");
            var Q8;
            Q8=makeQuery(id+"F22.opExtrude","SWEPT_BODY",BODY,{"disambiguationData":[OSD([sQuery(id+"F0.wireOp",EDGE,"E56.bottom"),sQuery(id+"F0.wireOp",EDGE,"E56.top"),sQuery(id+"F0.wireOp",EDGE,"E56.left"),sQuery(id+"F0.wireOp",EDGE,"E56.right")])]});
            var Q9;
            Q9=makeQuery(id+"F22.opExtrude","SWEPT_BODY",BODY,{"disambiguationData":[OSD([sQuery(id+"F0.wireOp",EDGE,"E53.bottom"),sQuery(id+"F0.wireOp",EDGE,"E53.top"),sQuery(id+"F0.wireOp",EDGE,"E53.left"),sQuery(id+"F0.wireOp",EDGE,"E53.right")])]});
            var Q10;
            Q10=makeQuery(id+"F22.opExtrude","SWEPT_BODY",BODY,{"disambiguationData":[OSD([sQuery(id+"F0.wireOp",EDGE,"E55.top"),sQuery(id+"F0.wireOp",EDGE,"E55.left"),sQuery(id+"F0.wireOp",EDGE,"E55.right"),sQuery(id+"F0.wireOp",EDGE,"E57")])]});
            var Q11;
            Q11=makeQuery(id+"F22.opExtrude","SWEPT_BODY",BODY,{"disambiguationData":[OSD([sQuery(id+"F0.wireOp",EDGE,"E54.bottom"),sQuery(id+"F0.wireOp",EDGE,"E54.top"),sQuery(id+"F0.wireOp",EDGE,"E54.left"),sQuery(id+"F0.wireOp",EDGE,"E54.right")])]});
            hole(context, id + "F23", {"style" : HoleStyle.SIMPLE, "endStyle" : HoleEndStyle.THROUGH, "oppositeDirection" : true, "holeDiameter" : 6.6 * mm, "locations" : qUnion([Q0, Q1, Q2, Q3, Q4, Q5, Q6, Q7]), "scope" : qUnion([Q8, Q9, Q10, Q11]), "isTappedThrough" : true});
        }
        {
            var Q0;
            Q0=makeQuery(id+"F22.opExtrude","CAP_EDGE",EDGE,{"disambiguationData":[OSD([sQuery(id+"F0.wireOp",EDGE,"E56.right")])],"isStart":false});
            var Q1;
            Q1=makeQuery(id+"F22.opExtrude","CAP_EDGE",EDGE,{"disambiguationData":[OSD([sQuery(id+"F0.wireOp",EDGE,"E56.left")])],"isStart":false});
            var Q2;
            Q2=makeQuery(id+"F22.opExtrude","CAP_EDGE",EDGE,{"disambiguationData":[OSD([sQuery(id+"F0.wireOp",EDGE,"E56.bottom")])],"isStart":false});
            var Q3;
            Q3=makeQuery(id+"F22.opExtrude","CAP_EDGE",EDGE,{"disambiguationData":[OSD([sQuery(id+"F0.wireOp",EDGE,"E56.top")])],"isStart":false});
            var Q4;
            Q4=makeQuery(id+"F22.opExtrude","CAP_EDGE",EDGE,{"disambiguationData":[OSD([sQuery(id+"F0.wireOp",EDGE,"E57")])],"isStart":false});
            var Q5;
            Q5=makeQuery(id+"F22.opExtrude","CAP_EDGE",EDGE,{"disambiguationData":[OSD([sQuery(id+"F0.wireOp",EDGE,"E55.top")])],"isStart":false});
            var Q6;
            Q6=makeQuery(id+"F22.opExtrude","CAP_EDGE",EDGE,{"disambiguationData":[OSD([sQuery(id+"F0.wireOp",EDGE,"E55.right")])],"isStart":false});
            var Q7;
            Q7=makeQuery(id+"F22.opExtrude","CAP_EDGE",EDGE,{"disambiguationData":[OSD([sQuery(id+"F0.wireOp",EDGE,"E55.left")])],"isStart":false});
            var Q8;
            Q8=makeQuery(id+"F22.opExtrude","CAP_EDGE",EDGE,{"disambiguationData":[OSD([sQuery(id+"F0.wireOp",EDGE,"E55.right")])],"isStart":true});
            var Q9;
            Q9=makeQuery(id+"F22.opExtrude","CAP_EDGE",EDGE,{"disambiguationData":[OSD([sQuery(id+"F0.wireOp",EDGE,"E57")])],"isStart":true});
            var Q10;
            Q10=makeQuery(id+"F22.opExtrude","CAP_EDGE",EDGE,{"disambiguationData":[OSD([sQuery(id+"F0.wireOp",EDGE,"E55.left")])],"isStart":true});
            var Q11;
            Q11=makeQuery(id+"F22.opExtrude","CAP_EDGE",EDGE,{"disambiguationData":[OSD([sQuery(id+"F0.wireOp",EDGE,"E55.top")])],"isStart":true});
            var Q12;
            Q12=makeQuery(id+"F22.opExtrude","CAP_EDGE",EDGE,{"disambiguationData":[OSD([sQuery(id+"F0.wireOp",EDGE,"E56.top")])],"isStart":true});
            var Q13;
            Q13=makeQuery(id+"F22.opExtrude","CAP_EDGE",EDGE,{"disambiguationData":[OSD([sQuery(id+"F0.wireOp",EDGE,"E56.left")])],"isStart":true});
            var Q14;
            Q14=makeQuery(id+"F22.opExtrude","CAP_EDGE",EDGE,{"disambiguationData":[OSD([sQuery(id+"F0.wireOp",EDGE,"E56.bottom")])],"isStart":true});
            var Q15;
            Q15=makeQuery(id+"F22.opExtrude","CAP_EDGE",EDGE,{"disambiguationData":[OSD([sQuery(id+"F0.wireOp",EDGE,"E56.right")])],"isStart":true});
            var Q16;
            Q16=makeQuery(id+"F22.opExtrude","CAP_EDGE",EDGE,{"disambiguationData":[OSD([sQuery(id+"F0.wireOp",EDGE,"E53.left")])],"isStart":true});
            var Q17;
            Q17=makeQuery(id+"F22.opExtrude","CAP_EDGE",EDGE,{"disambiguationData":[OSD([sQuery(id+"F0.wireOp",EDGE,"E53.bottom")])],"isStart":true});
            var Q18;
            Q18=makeQuery(id+"F22.opExtrude","CAP_EDGE",EDGE,{"disambiguationData":[OSD([sQuery(id+"F0.wireOp",EDGE,"E53.right")])],"isStart":true});
            var Q19;
            Q19=makeQuery(id+"F22.opExtrude","CAP_EDGE",EDGE,{"disambiguationData":[OSD([sQuery(id+"F0.wireOp",EDGE,"E53.left")])],"isStart":false});
            var Q20;
            Q20=makeQuery(id+"F22.opExtrude","CAP_EDGE",EDGE,{"disambiguationData":[OSD([sQuery(id+"F0.wireOp",EDGE,"E53.bottom")])],"isStart":false});
            var Q21;
            Q21=makeQuery(id+"F22.opExtrude","CAP_EDGE",EDGE,{"disambiguationData":[OSD([sQuery(id+"F0.wireOp",EDGE,"E53.top")])],"isStart":false});
            var Q22;
            Q22=makeQuery(id+"F22.opExtrude","CAP_EDGE",EDGE,{"disambiguationData":[OSD([sQuery(id+"F0.wireOp",EDGE,"E53.right")])],"isStart":false});
            var Q23;
            Q23=makeQuery(id+"F22.opExtrude","CAP_EDGE",EDGE,{"disambiguationData":[OSD([sQuery(id+"F0.wireOp",EDGE,"E54.top")])],"isStart":false});
            var Q24;
            Q24=makeQuery(id+"F22.opExtrude","CAP_EDGE",EDGE,{"disambiguationData":[OSD([sQuery(id+"F0.wireOp",EDGE,"E54.top")])],"isStart":true});
            var Q25;
            Q25=makeQuery(id+"F22.opExtrude","CAP_EDGE",EDGE,{"disambiguationData":[OSD([sQuery(id+"F0.wireOp",EDGE,"E54.bottom")])],"isStart":false});
            var Q26;
            Q26=makeQuery(id+"F22.opExtrude","CAP_EDGE",EDGE,{"disambiguationData":[OSD([sQuery(id+"F0.wireOp",EDGE,"E54.right")])],"isStart":false});
            var Q27;
            Q27=makeQuery(id+"F22.opExtrude","CAP_EDGE",EDGE,{"disambiguationData":[OSD([sQuery(id+"F0.wireOp",EDGE,"E54.bottom")])],"isStart":true});
            var Q28;
            Q28=makeQuery(id+"F22.opExtrude","CAP_EDGE",EDGE,{"disambiguationData":[OSD([sQuery(id+"F0.wireOp",EDGE,"E54.right")])],"isStart":true});
            fillet(context, id + "F24", {"entities" : qUnion([Q0, Q1, Q2, Q3, Q4, Q5, Q6, Q7, Q8, Q9, Q10, Q11, Q12, Q13, Q14, Q15, Q16, Q17, Q18, Q19, Q20, Q21, Q22, Q23, Q24, Q25, Q26, Q27, Q28]), "radius" : 5.08 * mm, "tangentPropagation" : true, "allowEdgeOverflow" : false});
        }
    });
